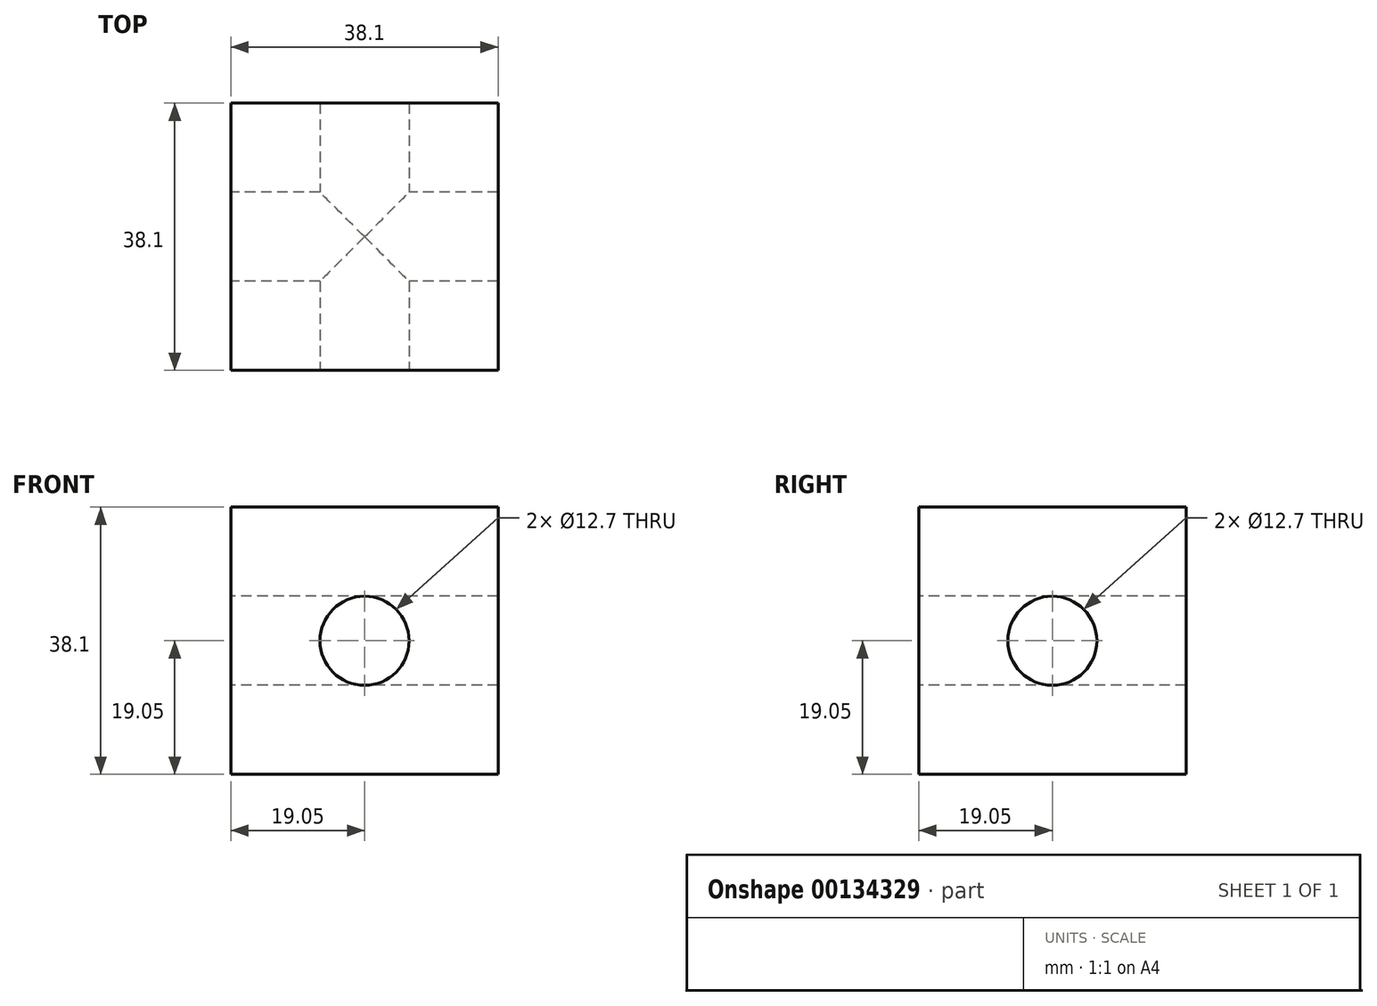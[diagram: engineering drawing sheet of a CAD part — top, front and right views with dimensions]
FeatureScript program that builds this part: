
annotation { "Feature Type Name" : "Feature", "Feature Type Description" : "" }
export const myFeature = defineFeature(function(context is Context, id is Id, definition is map)
    precondition{}
    {
        {
            var Q0;
            Q0=qCreatedBy(makeId("Front.planeOp"),FACE);
            var sketch = newSketch(context, id + "F0", { "sketchPlane" : qUnion([Q0])});
            skLineSegment(sketch, "E0.bottom", {"start": v(19.05, 19.05) * mm, "end": v(-19.05, 19.05) * mm});
            skLineSegment(sketch, "E0.top", {"start": v(19.05, -19.05) * mm, "end": v(-19.05, -19.05) * mm});
            skLineSegment(sketch, "E0.left", {"start": v(19.05, 19.05) * mm, "end": v(19.05, -19.05) * mm});
            skLineSegment(sketch, "E0.right", {"start": v(-19.05, 19.05) * mm, "end": v(-19.05, -19.05) * mm});
            skPoint(sketch, "E0.middle", {"position": v(0, 0) * mm});
            skSolve(sketch);
        }
        {
            var Q0;
            Q0=makeQuery(id+"F0.imprint","IMPRINT",FACE,{"disambiguationData":[TD([[makeQuery(id+"F0.imprint","IMPRINT",EDGE,{"derivedFrom":sQuery(id+"F0.wireOp",EDGE,"E0.bottom")}),1.0]])]});
            extrude(context, id + "F1", {"entities" : qUnion([Q0]), "endBound" : BoundingType.SYMMETRIC, "depth" : 38.1 * mm});
        }
        {
            var Q0;
            Q0=makeQuery(id+"F1.opExtrude","CAP_FACE",FACE,{"disambiguationData":[OSD([sQuery(id+"F0.wireOp",EDGE,"E0.bottom"),sQuery(id+"F0.wireOp",EDGE,"E0.top"),sQuery(id+"F0.wireOp",EDGE,"E0.left"),sQuery(id+"F0.wireOp",EDGE,"E0.right")])],"isStart":false});
            var sketch = newSketch(context, id + "F2", { "sketchPlane" : qUnion([Q0])});
            skPoint(sketch, "E1", {"position": v(0, 0) * mm});
            skSolve(sketch);
        }
        {
            var Q0;
            Q0=makeQuery(id+"F1.opExtrude","SWEPT_FACE",FACE,{"disambiguationData":[OSD([sQuery(id+"F0.wireOp",EDGE,"E0.right")])]});
            var sketch = newSketch(context, id + "F3", { "sketchPlane" : qUnion([Q0])});
            skPoint(sketch, "E2", {"position": v(0, 0) * mm});
            skSolve(sketch);
        }
        {
            var Q0;
            Q0=sQuery(id+"F3.wireOp",VERTEX,"E2");
            var Q1;
            Q1=sQuery(id+"F2.wireOp",VERTEX,"E1");
            var Q2;
            Q2=makeQuery(id+"F1.opExtrude","SWEPT_BODY",BODY,{"disambiguationData":[OSD([sQuery(id+"F0.wireOp",EDGE,"E0.bottom"),sQuery(id+"F0.wireOp",EDGE,"E0.top"),sQuery(id+"F0.wireOp",EDGE,"E0.left"),sQuery(id+"F0.wireOp",EDGE,"E0.right")])]});
            hole(context, id + "F4", {"style" : HoleStyle.SIMPLE, "endStyle" : HoleEndStyle.THROUGH, "holeDiameter" : 12.7 * mm, "locations" : qUnion([Q0, Q1]), "scope" : qUnion([Q2]), "isTappedThrough" : true});
        }
    });
